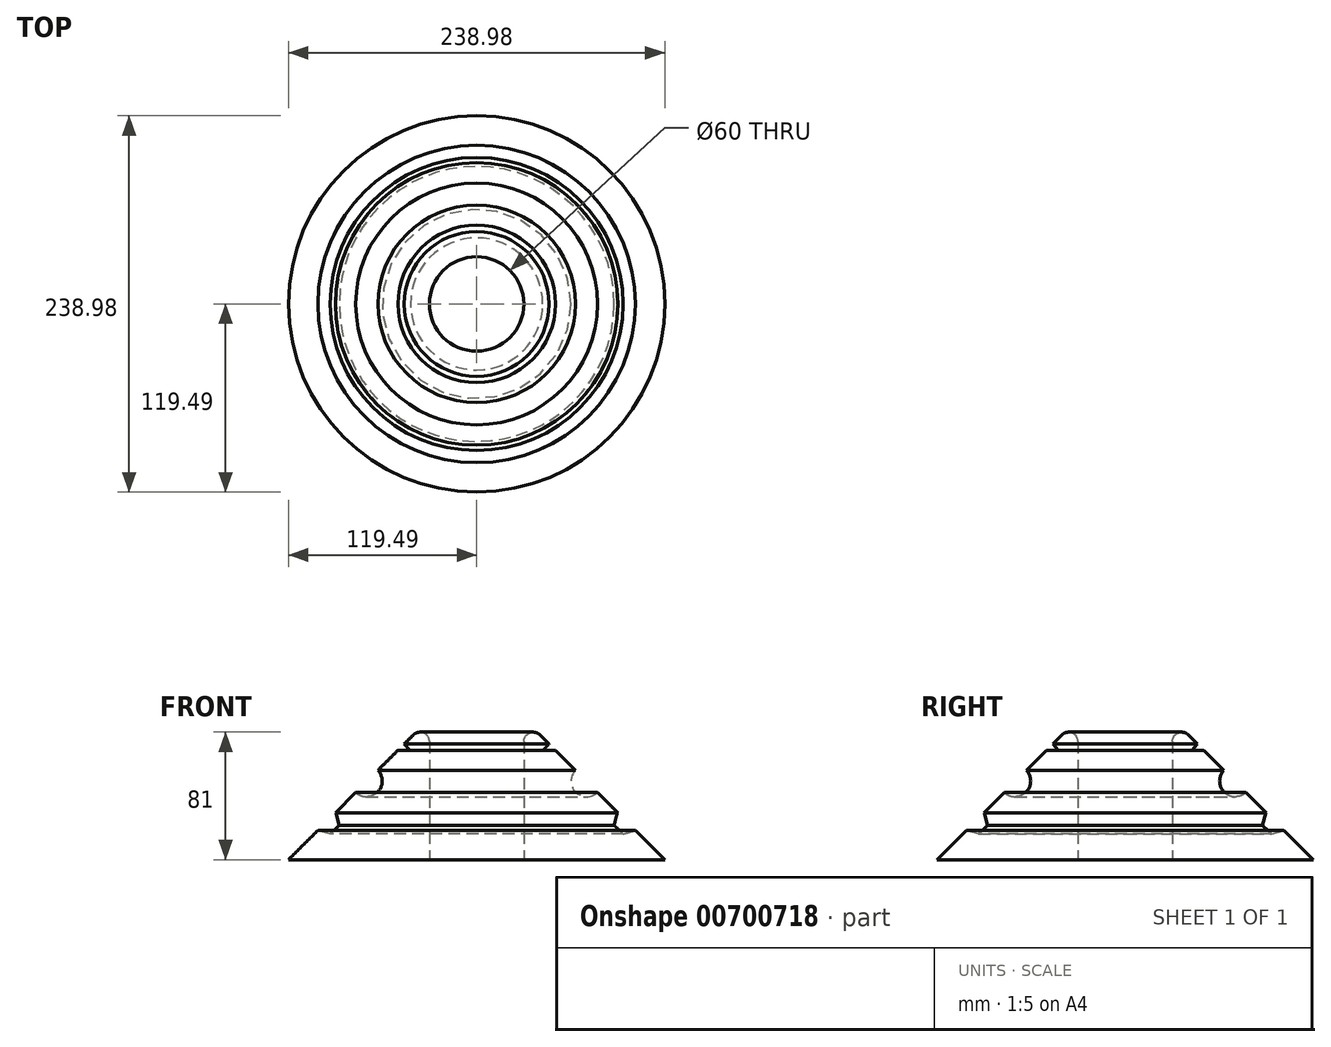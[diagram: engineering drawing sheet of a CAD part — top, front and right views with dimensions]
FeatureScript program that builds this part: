
annotation { "Feature Type Name" : "Feature", "Feature Type Description" : "" }
export const myFeature = defineFeature(function(context is Context, id is Id, definition is map)
    precondition{}
    {
        {
            var Q0;
            Q0=qCreatedBy(makeId("Front.planeOp"),FACE);
            var sketch = newSketch(context, id + "F0", { "sketchPlane" : qUnion([Q0])});
            skLineSegment(sketch, "E0", {"start": v(-30, 0) * mm, "end": v(-30, 75) * mm});
            skLineSegment(sketch, "E1", {"start": v(-40.24, 79.24) * mm, "end": v(-119.49, 0) * mm});
            skLineSegment(sketch, "E2", {"start": v(-119.49, 0) * mm, "end": v(-30, 0) * mm});
            skArc(sketch, "E3.filletArc", {"start": v(-30, 75) * mm, "mid": v(-33.7, 80.54) * mm, "end": v(-40.24, 79.24) * mm});
            skLineSegment(sketch, "E4", {"start": v(0, 0) * mm, "end": v(0, 89.2) * mm, "construction": true});
            skSolve(sketch);
        }
        {
            var Q0;
            Q0=makeQuery(id+"F0.imprint","IMPRINT",FACE,{"disambiguationData":[TD([[makeQuery(id+"F0.imprint","IMPRINT",EDGE,{"derivedFrom":sQuery(id+"F0.wireOp",EDGE,"E0")}),1.0]])]});
            var Q1;
            Q1 = qConstructionFilter(qBodyType(qCreatedBy(id + "F0" ,EDGE), BodyType.WIRE), ConstructionObject.NO);
            var Q2;
            Q2=sQuery(id+"F0.wireOp",EDGE,"E4");
            revolve(context, id + "F1", {"entities" : qUnion([Q0]), "surfaceEntities" : qUnion([Q1]), "axis" : qUnion([Q2]), "revolveType" : RevolveType.FULL});
        }
        {
            var Q0;
            Q0=qCreatedBy(makeId("Front.planeOp"),FACE);
            var sketch = newSketch(context, id + "F2", { "sketchPlane" : qUnion([Q0])});
            skCircle(sketch, "E5", {"center": v(-70, 50) * mm, "radius": 10 * mm});
            skLineSegment(sketch, "E6", {"start": v(0, 0) * mm, "end": v(0, 88.45) * mm, "construction": true});
            skSolve(sketch);
        }
        {
            var Q0;
            Q0=makeQuery(id+"F2.imprint","IMPRINT",FACE,{"disambiguationData":[TD([[makeQuery(id+"F2.imprint","IMPRINT",EDGE,{"derivedFrom":sQuery(id+"F2.wireOp",EDGE,"E5")}),1.0]])]});
            var Q1;
            Q1=sQuery(id+"F2.wireOp",EDGE,"E5");
            var Q2;
            Q2=sQuery(id+"F2.wireOp",EDGE,"E6");
            revolve(context, id + "F3", {"operationType" : NewBodyOperationType.REMOVE, "entities" : qUnion([Q0]), "surfaceEntities" : qUnion([Q1]), "axis" : qUnion([Q2]), "revolveType" : RevolveType.FULL, "oppositeDirection" : true});
        }
        {
            var Q0;
            Q0=qCreatedBy(makeId("Front.planeOp"),FACE);
            var sketch = newSketch(context, id + "F4", { "sketchPlane" : qUnion([Q0])});
            skCircle(sketch, "E7.cCircle", {"center": v(-95, 24.06) * mm, "radius": 6.93 * mm, "construction": true});
            skLineSegment(sketch, "E7.0", {"start": v(-87.31, 21.85) * mm, "end": v(-93.07, 16.3) * mm});
            skLineSegment(sketch, "E7.1", {"start": v(-93.07, 16.3) * mm, "end": v(-100.76, 18.5) * mm});
            skLineSegment(sketch, "E7.2", {"start": v(-100.76, 18.5) * mm, "end": v(-102.69, 26.27) * mm});
            skLineSegment(sketch, "E7.3", {"start": v(-102.69, 26.27) * mm, "end": v(-96.93, 31.82) * mm});
            skLineSegment(sketch, "E7.4", {"start": v(-96.93, 31.82) * mm, "end": v(-89.24, 29.61) * mm});
            skLineSegment(sketch, "E7.5", {"start": v(-89.24, 29.61) * mm, "end": v(-87.31, 21.85) * mm});
            skPoint(sketch, "E7.0.midPoint", {"position": v(-90.2, 19.07) * mm});
            skLineSegment(sketch, "E8", {"start": v(0, 0) * mm, "end": v(0, 89.44) * mm, "construction": true});
            skSolve(sketch);
        }
        {
            var Q0;
            Q0=makeQuery(id+"F4.imprint","IMPRINT",FACE,{"disambiguationData":[TD([[makeQuery(id+"F4.imprint","IMPRINT",EDGE,{"derivedFrom":sQuery(id+"F4.wireOp",EDGE,"E7.0")}),-1.0]])]});
            var Q1;
            Q1=sQuery(id+"F4.wireOp",EDGE,"E8");
            var Q2;
            Q2=sQuery(id+"F4.wireOp",EDGE,"E8");
            revolve(context, id + "F5", {"operationType" : NewBodyOperationType.REMOVE, "entities" : qUnion([Q0]), "surfaceEntities" : qUnion([Q1]), "axis" : qUnion([Q2]), "revolveType" : RevolveType.FULL, "oppositeDirection" : true});
        }
        {
            var Q0;
            Q0=qCreatedBy(makeId("Front.planeOp"),FACE);
            var sketch = newSketch(context, id + "F6", { "sketchPlane" : qUnion([Q0])});
            skLineSegment(sketch, "E9", {"start": v(-50.64, 69.5) * mm, "end": v(-41.95, 69.1) * mm});
            skLineSegment(sketch, "E10", {"start": v(-41.95, 69.1) * mm, "end": v(-50.24, 78.2) * mm});
            skLineSegment(sketch, "E11", {"start": v(-50.24, 78.2) * mm, "end": v(-50.64, 69.5) * mm});
            skLineSegment(sketch, "E12", {"start": v(0, 0) * mm, "end": v(0, 89.8) * mm, "construction": true});
            skSolve(sketch);
        }
        {
            var Q0;
            Q0=makeQuery(id+"F6.imprint","IMPRINT",FACE,{"disambiguationData":[TD([[makeQuery(id+"F6.imprint","IMPRINT",EDGE,{"derivedFrom":sQuery(id+"F6.wireOp",EDGE,"E9")}),1.0]])]});
            var Q1;
            Q1=sQuery(id+"F6.wireOp",EDGE,"E12");
            var Q2;
            Q2=sQuery(id+"F6.wireOp",EDGE,"E12");
            revolve(context, id + "F7", {"operationType" : NewBodyOperationType.REMOVE, "entities" : qUnion([Q0]), "surfaceEntities" : qUnion([Q1]), "axis" : qUnion([Q2]), "revolveType" : RevolveType.FULL, "oppositeDirection" : true});
        }
    });
